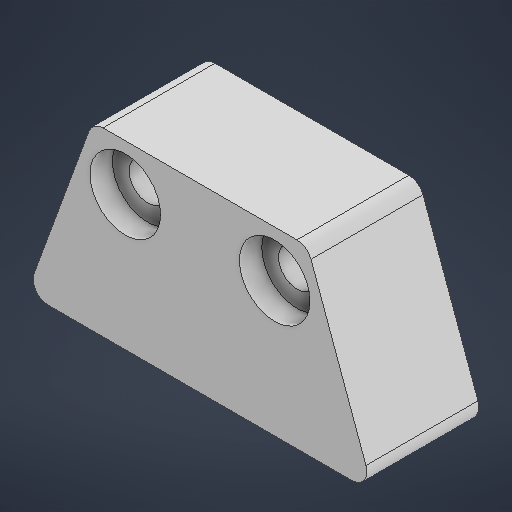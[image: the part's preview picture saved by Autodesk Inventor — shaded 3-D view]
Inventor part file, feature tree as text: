
AUTODESK INVENTOR PART (.ipt)
format: ipt  version: 2025.3 (Build 293356030, 356C)  size: 218,112 bytes
history: native  units: mm
features: extrude x2, sketch x1
ambient origin geometry x8: Origin, YZ Plane, XZ Plane, XY Plane, X Axis, Y Axis, Z Axis, Center Point
bodies: Solid1 (feature_tree)
feature tree (3):
  sketch  "Sketch1"  dims[d1=18.9mm d3=3.0mm d4=36.0mm d7=10.0mm d8=40.0mm d10=4.0mm d11=12.5mm d12=12.217305mm d13=30.0mm d14=0.0mm d15=18.0mm d16=0.0mm]
  extrude  "Extrusion1"  Depth=18.0mm
  extrude  "Extrusion2"  Depth=18.0mm
